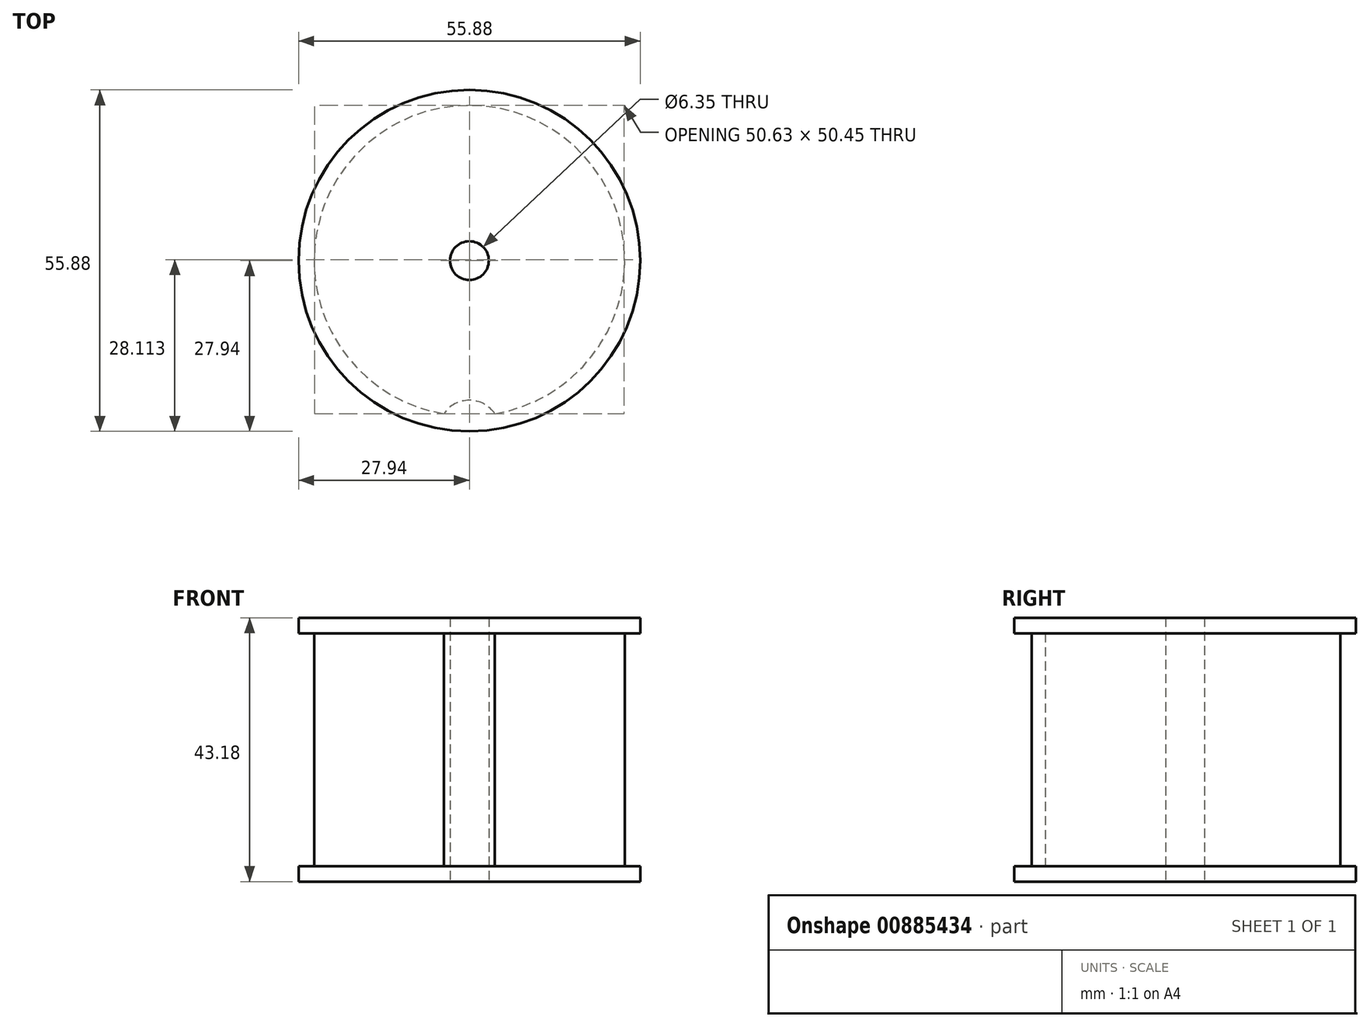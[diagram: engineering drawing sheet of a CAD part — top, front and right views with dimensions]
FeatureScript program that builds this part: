
annotation { "Feature Type Name" : "Feature", "Feature Type Description" : "" }
export const myFeature = defineFeature(function(context is Context, id is Id, definition is map)
    precondition{}
    {
        {
            var Q0;
            Q0=qCreatedBy(makeId("Top.planeOp"),FACE);
            var sketch = newSketch(context, id + "F0", { "sketchPlane" : qUnion([Q0])});
            skCircle(sketch, "E0", {"center": v(0, 0) * mm, "radius": 25.4 * mm});
            skSolve(sketch);
        }
        {
            var Q0;
            Q0=qSketchRegion(id+"F0",true);
            extrude(context, id + "F1", {"entities" : qUnion([Q0]), "endBound" : BoundingType.SYMMETRIC, "depth" : 38.1 * mm, "offsetDistance" : 25.4 * mm});
        }
        {
            var Q0;
            Q0=makeQuery(id+"F1.opExtrude","CAP_FACE",FACE,{"disambiguationData":[OSD([sQuery(id+"F0.wireOp",EDGE,"E0")])],"isStart":false});
            var sketch = newSketch(context, id + "F2", { "sketchPlane" : qUnion([Q0])});
            skCircle(sketch, "E1", {"center": v(0, 0) * mm, "radius": 27.94 * mm});
            skSolve(sketch);
        }
        {
            var Q0;
            Q0=makeQuery(id+"F2.imprint","IMPRINT",FACE,{"disambiguationData":[TD([[makeQuery(id+"F2.imprint","IMPRINT",EDGE,{"derivedFrom":sQuery(id+"F2.wireOp",EDGE,"E1")}),1.0]])]});
            var Q1;
            Q1=makeQuery(id+"F2.imprint","IMPRINT",FACE,{"disambiguationData":[TD([[makeQuery(id+"F2.imprint","IMPRINT",EDGE,{"derivedFrom":makeQuery(id+"F1.opExtrude","CAP_EDGE",EDGE,{"disambiguationData":[OSD([sQuery(id+"F0.wireOp",EDGE,"E0")])],"isStart":false})}),1.0]])]});
            extrude(context, id + "F3", {"entities" : qUnion([Q0, Q1]), "operationType" : NewBodyOperationType.ADD, "depth" : 2.54 * mm, "offsetDistance" : 25.4 * mm});
        }
        {
            var Q0;
            Q0=makeQuery(id+"F1.opExtrude","CAP_FACE",FACE,{"disambiguationData":[OSD([sQuery(id+"F0.wireOp",EDGE,"E0")])],"isStart":true});
            var sketch = newSketch(context, id + "F4", { "sketchPlane" : qUnion([Q0])});
            skArc(sketch, "E2", {"start": v(-4.18, 25.05) * mm, "mid": v(0, 22.86) * mm, "end": v(4.18, 25.05) * mm});
            skSolve(sketch);
        }
        {
            var Q0;
            {var subQ0=sQuery(id+"F4.wireOp",EDGE,"E2");Q0=makeQuery(id+"F4.imprint","IMPRINT",FACE,{"disambiguationData":[TD([[makeQuery(id+"F4.imprint","IMPRINT",EDGE,{"derivedFrom":subQ0}),1.0]])]});}
            var Q1;
            Q1=makeQuery(id+"F3.opExtrude","CAP_FACE",FACE,{"disambiguationData":[OSD([sQuery(id+"F2.wireOp",EDGE,"E1")])],"isStart":true});
            extrude(context, id + "F5", {"entities" : qUnion([Q0]), "operationType" : NewBodyOperationType.REMOVE, "endBound" : BoundingType.UP_TO_SURFACE, "oppositeDirection" : true, "depth" : 25.4 * mm, "endBoundEntityFace" : qUnion([Q1]), "offsetDistance" : 25.4 * mm});
        }
        {
            var Q0;
            Q0=makeQuery(id+"F1.opExtrude","CAP_FACE",FACE,{"disambiguationData":[OSD([sQuery(id+"F0.wireOp",EDGE,"E0")])],"isStart":true});
            var sketch = newSketch(context, id + "F6", { "sketchPlane" : qUnion([Q0])});
            skCircle(sketch, "E3", {"center": v(0, 0) * mm, "radius": 27.94 * mm});
            skSolve(sketch);
        }
        {
            var Q0;
            Q0 = qSketchRegion(id + "F6", true);
            extrude(context, id + "F7", {"entities" : qUnion([Q0]), "operationType" : NewBodyOperationType.ADD, "depth" : 2.54 * mm, "offsetDistance" : 25.4 * mm});
        }
        {
            var Q0;
            Q0=makeQuery(id+"F7.opExtrude","CAP_FACE",FACE,{"disambiguationData":[OSD([sQuery(id+"F6.wireOp",EDGE,"E3")])],"isStart":false});
            var sketch = newSketch(context, id + "F8", { "sketchPlane" : qUnion([Q0])});
            skCircle(sketch, "E4", {"center": v(0, 0) * mm, "radius": 3.18 * mm});
            skSolve(sketch);
        }
        {
            var Q0;
            Q0=makeQuery(id+"F8.imprint","IMPRINT",FACE,{"disambiguationData":[TD([[makeQuery(id+"F8.imprint","IMPRINT",EDGE,{"derivedFrom":sQuery(id+"F8.wireOp",EDGE,"E4")}),1.0]])]});
            extrude(context, id + "F9", {"entities" : qUnion([Q0]), "operationType" : NewBodyOperationType.REMOVE, "endBound" : BoundingType.THROUGH_ALL, "oppositeDirection" : true, "depth" : 25.4 * mm, "offsetDistance" : 25.4 * mm});
        }
    });
